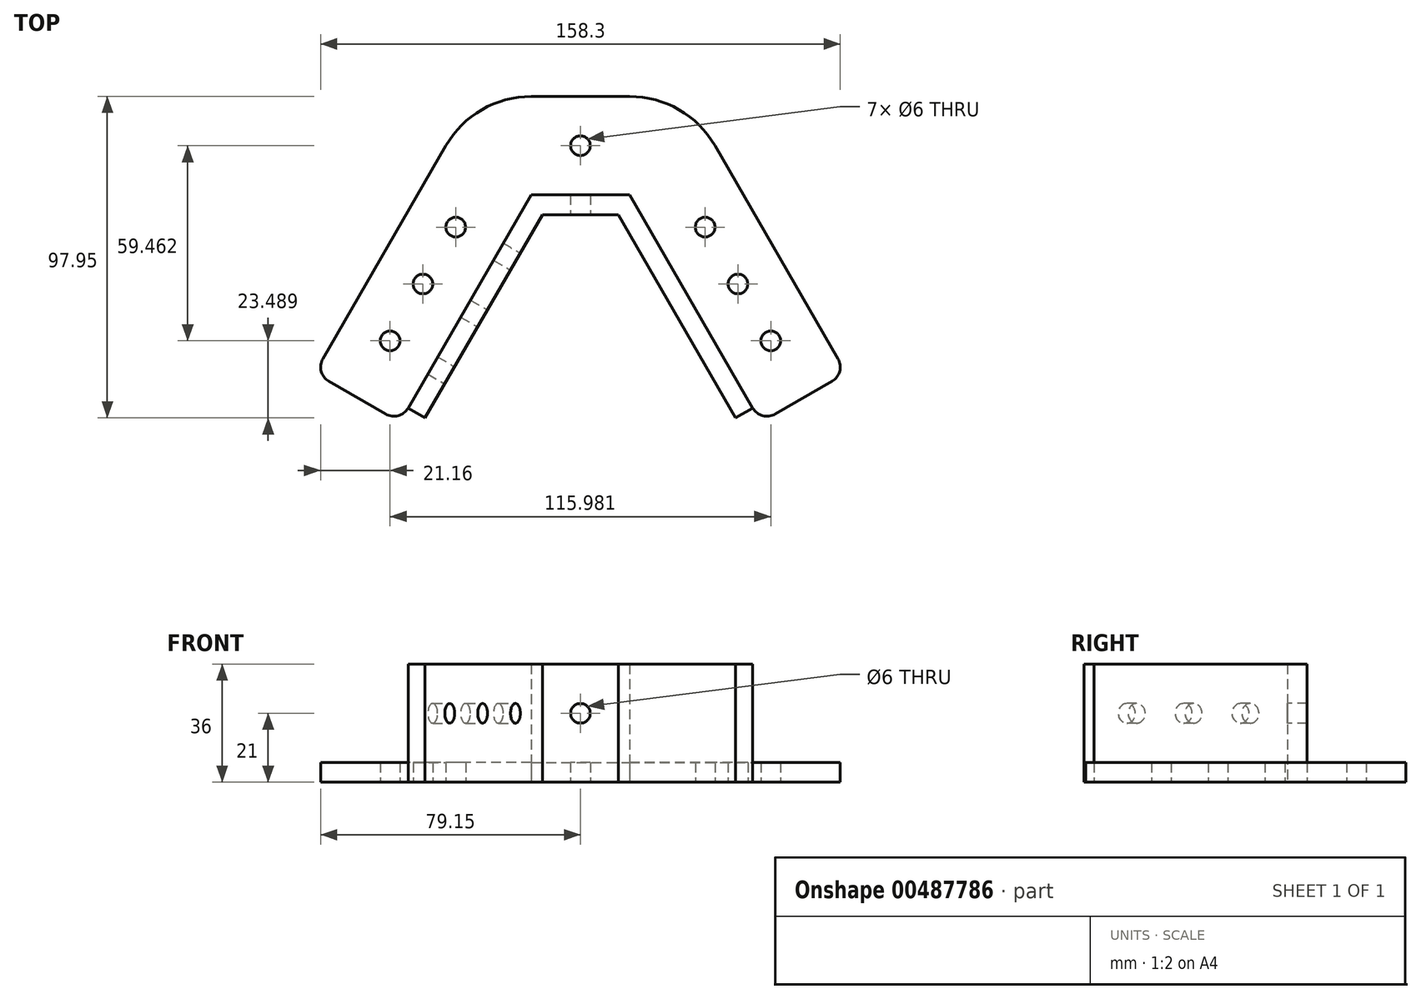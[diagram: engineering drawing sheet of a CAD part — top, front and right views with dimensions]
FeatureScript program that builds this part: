
annotation { "Feature Type Name" : "Feature", "Feature Type Description" : "" }
export const myFeature = defineFeature(function(context is Context, id is Id, definition is map)
    precondition{}
    {
        {
            var Q0;
            Q0=qCreatedBy(makeId("Top.planeOp"),FACE);
            var sketch = newSketch(context, id + "F0", { "sketchPlane" : qUnion([Q0])});
            skLineSegment(sketch, "E0.bottom", {"start": v(-15, 36.51) * mm, "end": v(15, 36.51) * mm});
            skLineSegment(sketch, "E0.top", {"start": v(-15, 6.51) * mm, "end": v(15, 6.51) * mm});
            skLineSegment(sketch, "E1", {"start": v(-15, 6.51) * mm, "end": v(-55, -62.77) * mm});
            skLineSegment(sketch, "E2", {"start": v(-55, -62.77) * mm, "end": v(-80.98, -47.77) * mm});
            skLineSegment(sketch, "E3", {"start": v(-80.98, -47.77) * mm, "end": v(-40.98, 21.51) * mm});
            skLineSegment(sketch, "E4.MirrorCS", {"start": v(15, 6.51) * mm, "end": v(55, -62.77) * mm});
            skLineSegment(sketch, "E5.MirrorCS", {"start": v(80.98, -47.77) * mm, "end": v(40.98, 21.51) * mm});
            skLineSegment(sketch, "E6.MirrorCS", {"start": v(55, -62.77) * mm, "end": v(80.98, -47.77) * mm});
            skArc(sketch, "E7", {"start": v(-40.98, 21.51) * mm, "mid": v(-30, 32.5) * mm, "end": v(-15, 36.51) * mm});
            skArc(sketch, "E8.MirrorCS", {"start": v(40.98, 21.51) * mm, "mid": v(30, 32.5) * mm, "end": v(15, 36.51) * mm});
            skCircle(sketch, "E9", {"center": v(0, 21.51) * mm, "radius": 3 * mm});
            skLineSegment(sketch, "E10", {"start": v(-68, -55.27) * mm, "end": v(-28, 14.01) * mm, "construction": true});
            skCircle(sketch, "E11", {"center": v(-58, -37.95) * mm, "radius": 3 * mm});
            skCircle(sketch, "E12", {"center": v(-48, -20.63) * mm, "radius": 3 * mm});
            skCircle(sketch, "E13", {"center": v(-38, -3.31) * mm, "radius": 3 * mm});
            skLineSegment(sketch, "E14.MirrorCS", {"start": v(68, -55.27) * mm, "end": v(28, 14.01) * mm, "construction": true});
            skCircle(sketch, "E15.MirrorC", {"center": v(38, -3.31) * mm, "radius": 3 * mm});
            skCircle(sketch, "E16.MirrorC", {"center": v(48, -20.63) * mm, "radius": 3 * mm});
            skCircle(sketch, "E17.MirrorC", {"center": v(58, -37.95) * mm, "radius": 3 * mm});
            skSolve(sketch);
        }
        {
            var Q0;
            Q0=makeQuery(id+"F0.imprint","IMPRINT",FACE,{"disambiguationData":[TD([[makeQuery(id+"F0.imprint","IMPRINT",EDGE,{"derivedFrom":sQuery(id+"F0.wireOp",EDGE,"E0.bottom")}),-1.0]])]});
            extrude(context, id + "F1", {"entities" : qUnion([Q0]), "depth" : 6 * mm});
        }
        {
            var Q0;
            Q0=makeQuery(id+"F1.opExtrude","SWEPT_EDGE",EDGE,{"disambiguationData":[OSD([sQuery(id+"F0.wireOp",EDGE,"E5.MirrorCS"),sQuery(id+"F0.wireOp",EDGE,"E6.MirrorCS")])]});
            fillet(context, id + "F2", {"entities" : qUnion([Q0]), "radius" : 5 * mm, "tangentPropagation" : true, "allowEdgeOverflow" : false});
        }
        {
            var Q0;
            Q0=makeQuery(id+"F1.opExtrude","SWEPT_EDGE",EDGE,{"disambiguationData":[OSD([sQuery(id+"F0.wireOp",EDGE,"E4.MirrorCS"),sQuery(id+"F0.wireOp",EDGE,"E6.MirrorCS")])]});
            fillet(context, id + "F3", {"entities" : qUnion([Q0]), "radius" : 5 * mm, "tangentPropagation" : true, "allowEdgeOverflow" : false});
        }
        {
            var Q0;
            Q0=makeQuery(id+"F1.opExtrude","SWEPT_EDGE",EDGE,{"disambiguationData":[OSD([sQuery(id+"F0.wireOp",EDGE,"E1"),sQuery(id+"F0.wireOp",EDGE,"E2")])]});
            fillet(context, id + "F4", {"entities" : qUnion([Q0]), "radius" : 5 * mm, "tangentPropagation" : true, "allowEdgeOverflow" : false});
        }
        {
            var Q0;
            Q0=makeQuery(id+"F1.opExtrude","SWEPT_EDGE",EDGE,{"disambiguationData":[OSD([sQuery(id+"F0.wireOp",EDGE,"E2"),sQuery(id+"F0.wireOp",EDGE,"E3")])]});
            fillet(context, id + "F5", {"entities" : qUnion([Q0]), "radius" : 5 * mm, "tangentPropagation" : true, "allowEdgeOverflow" : false});
        }
        {
            var Q0;
            Q0=makeQuery(id+"F1.opExtrude","CAP_FACE",FACE,{"disambiguationData":[OSD([sQuery(id+"F0.wireOp",EDGE,"E0.bottom"),sQuery(id+"F0.wireOp",EDGE,"E0.top"),sQuery(id+"F0.wireOp",EDGE,"E1"),sQuery(id+"F0.wireOp",EDGE,"E2"),sQuery(id+"F0.wireOp",EDGE,"E3"),sQuery(id+"F0.wireOp",EDGE,"E4.MirrorCS"),sQuery(id+"F0.wireOp",EDGE,"E5.MirrorCS"),sQuery(id+"F0.wireOp",EDGE,"E6.MirrorCS"),sQuery(id+"F0.wireOp",EDGE,"E7"),sQuery(id+"F0.wireOp",EDGE,"E8.MirrorCS"),sQuery(id+"F0.wireOp",EDGE,"E9"),sQuery(id+"F0.wireOp",EDGE,"E11"),sQuery(id+"F0.wireOp",EDGE,"E12"),sQuery(id+"F0.wireOp",EDGE,"E13"),sQuery(id+"F0.wireOp",EDGE,"E15.MirrorC"),sQuery(id+"F0.wireOp",EDGE,"E16.MirrorC"),sQuery(id+"F0.wireOp",EDGE,"E17.MirrorC")])],"isStart":false});
            var sketch = newSketch(context, id + "F6", { "sketchPlane" : qUnion([Q0])});
            skLineSegment(sketch, "E18", {"start": v(15, 6.51) * mm, "end": v(-15, 6.51) * mm});
            skLineSegment(sketch, "E19", {"start": v(-15, 6.51) * mm, "end": v(-52.5, -58.44) * mm});
            skLineSegment(sketch, "E20", {"start": v(15, 6.51) * mm, "end": v(52.5, -58.44) * mm});
            skLineSegment(sketch, "E21.0", {"start": v(-11.54, 0.51) * mm, "end": v(-47.3, -61.44) * mm});
            skLineSegment(sketch, "E21.1", {"start": v(11.54, 0.51) * mm, "end": v(-11.54, 0.51) * mm});
            skLineSegment(sketch, "E21.2", {"start": v(11.54, 0.51) * mm, "end": v(47.3, -61.44) * mm});
            skLineSegment(sketch, "E22", {"start": v(-47.3, -61.44) * mm, "end": v(-52.5, -58.44) * mm});
            skLineSegment(sketch, "E23", {"start": v(47.3, -61.44) * mm, "end": v(52.5, -58.44) * mm});
            skSolve(sketch);
        }
        {
            var Q0;
            Q0=makeQuery(id+"F6.imprint","IMPRINT",FACE,{"disambiguationData":[TD([[makeQuery(id+"F6.imprint","IMPRINT",EDGE,{"derivedFrom":sQuery(id+"F6.wireOp",EDGE,"E18")}),-1.0]])]});
            extrude(context, id + "F7", {"entities" : qUnion([Q0]), "depth" : 30 * mm, "hasSecondDirection" : true, "secondDirectionOppositeDirection" : true, "secondDirectionDepth" : 6 * mm});
        }
        {
            var Q0;
            Q0=makeQuery(id+"F7.opExtrude","SWEPT_FACE",FACE,{"disambiguationData":[OSD([sQuery(id+"F6.wireOp",EDGE,"E21.0")])]});
            var sketch = newSketch(context, id + "F8", { "sketchPlane" : qUnion([Q0])});
            skCircle(sketch, "E24", {"center": v(-61.86, 21) * mm, "radius": 3 * mm});
            skCircle(sketch, "E25", {"center": v(-41.86, 21) * mm, "radius": 3 * mm});
            skCircle(sketch, "E26", {"center": v(-21.86, 21) * mm, "radius": 3 * mm});
            skSolve(sketch);
        }
        {
            var Q0;
            Q0=makeQuery(id+"F8.imprint","IMPRINT",FACE,{"disambiguationData":[TD([[makeQuery(id+"F8.imprint","IMPRINT",EDGE,{"derivedFrom":sQuery(id+"F8.wireOp",EDGE,"E24")}),1.0]])]});
            var Q1;
            Q1=makeQuery(id+"F8.imprint","IMPRINT",FACE,{"disambiguationData":[TD([[makeQuery(id+"F8.imprint","IMPRINT",EDGE,{"derivedFrom":sQuery(id+"F8.wireOp",EDGE,"E25")}),1.0]])]});
            var Q2;
            Q2=makeQuery(id+"F8.imprint","IMPRINT",FACE,{"disambiguationData":[TD([[makeQuery(id+"F8.imprint","IMPRINT",EDGE,{"derivedFrom":sQuery(id+"F8.wireOp",EDGE,"E26")}),1.0]])]});
            extrude(context, id + "F9", {"entities" : qUnion([Q0, Q1, Q2]), "operationType" : NewBodyOperationType.REMOVE, "endBound" : BoundingType.THROUGH_ALL, "oppositeDirection" : true, "depth" : 25 * mm});
        }
        {
            var Q0;
            Q0=makeQuery(id+"F7.opExtrude","SWEPT_FACE",FACE,{"disambiguationData":[OSD([sQuery(id+"F6.wireOp",EDGE,"E21.1")])]});
            var sketch = newSketch(context, id + "F10", { "sketchPlane" : qUnion([Q0])});
            skCircle(sketch, "E27", {"center": v(0, 21) * mm, "radius": 3 * mm});
            skSolve(sketch);
        }
        {
            var Q0;
            Q0 = qSketchRegion(id + "F10", true);
            extrude(context, id + "F11", {"entities" : qUnion([Q0]), "operationType" : NewBodyOperationType.REMOVE, "endBound" : BoundingType.THROUGH_ALL, "oppositeDirection" : true, "depth" : 25 * mm});
        }
    });
